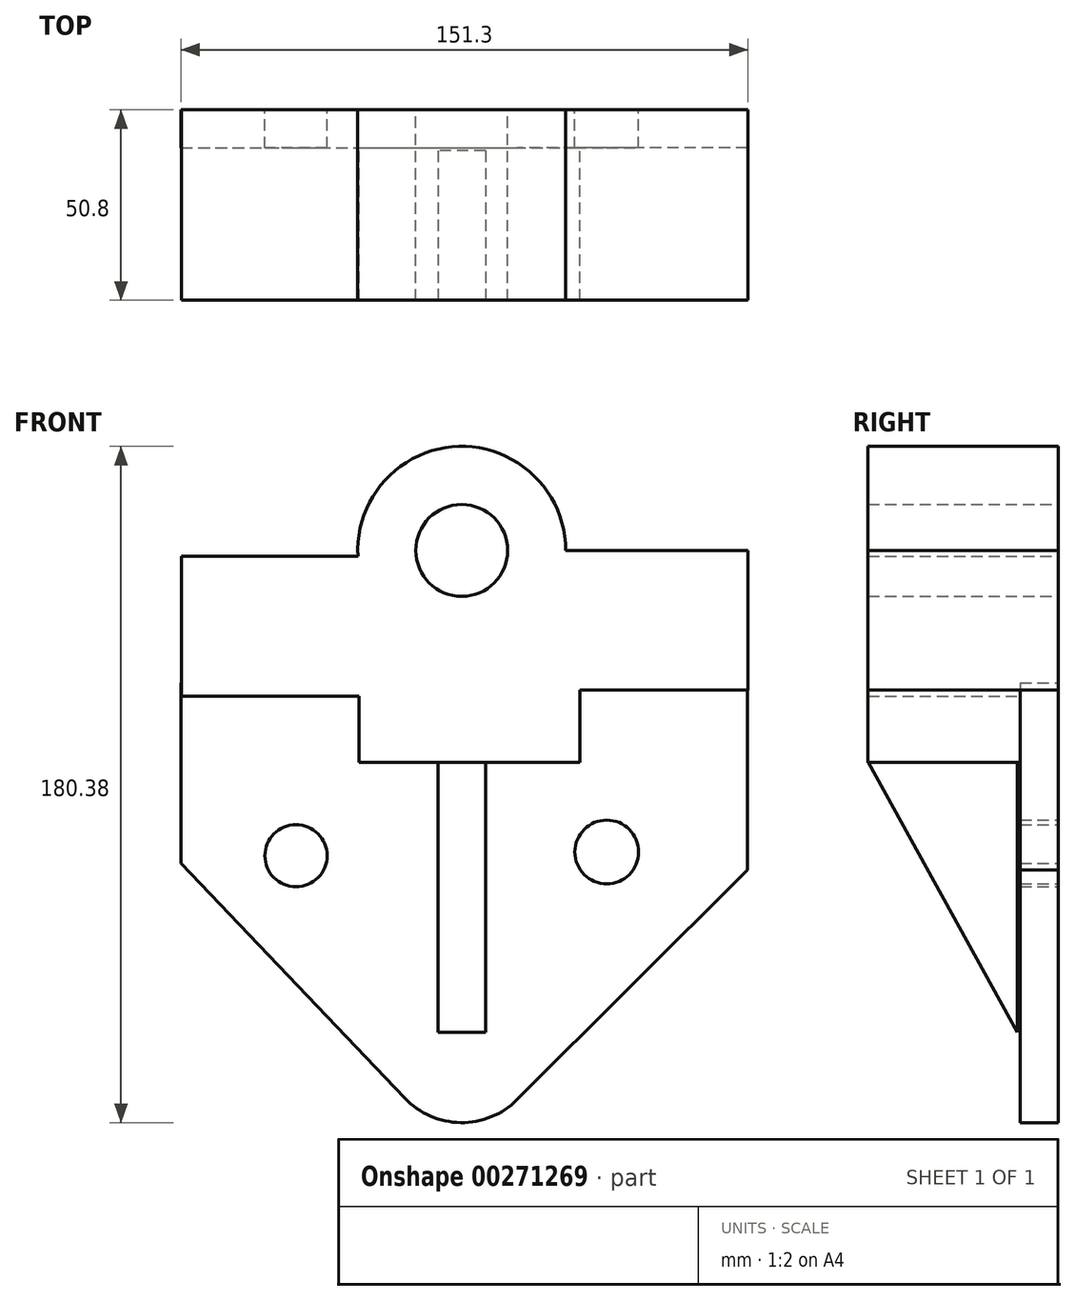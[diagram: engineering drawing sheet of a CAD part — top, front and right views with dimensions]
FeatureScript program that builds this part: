
annotation { "Feature Type Name" : "Feature", "Feature Type Description" : "" }
export const myFeature = defineFeature(function(context is Context, id is Id, definition is map)
    precondition{}
    {
        {
            var Q0;
            Q0=qCreatedBy(makeId("Front.planeOp"),FACE);
            var sketch = newSketch(context, id + "F0", { "sketchPlane" : qUnion([Q0])});
            skArc(sketch, "E0", {"start": v(27.74, 56.5) * mm, "mid": v(-0.75, 84.23) * mm, "end": v(-27.7, 54.99) * mm});
            skCircle(sketch, "E1", {"center": v(0, 56.5) * mm, "radius": 12.25 * mm});
            skLineSegment(sketch, "E2", {"start": v(27.74, 56.5) * mm, "end": v(76.4, 56.5) * mm});
            skLineSegment(sketch, "E3", {"start": v(76.4, 56.5) * mm, "end": v(76.4, 19.25) * mm});
            skLineSegment(sketch, "E4", {"start": v(76.4, 19.25) * mm, "end": v(31.51, 19.25) * mm});
            skLineSegment(sketch, "E5", {"start": v(31.51, 19.25) * mm, "end": v(31.51, 0) * mm});
            skLineSegment(sketch, "E6", {"start": v(31.51, 0) * mm, "end": v(0, 0) * mm});
            skLineSegment(sketch, "E7", {"start": v(-27.7, 54.99) * mm, "end": v(-74.78, 54.99) * mm});
            skLineSegment(sketch, "E8", {"start": v(-74.78, 54.99) * mm, "end": v(-74.78, 17.61) * mm});
            skLineSegment(sketch, "E9", {"start": v(-74.78, 17.61) * mm, "end": v(-27.36, 17.61) * mm});
            skLineSegment(sketch, "E10", {"start": v(-27.36, 17.61) * mm, "end": v(-27.36, 0) * mm});
            skLineSegment(sketch, "E11", {"start": v(-27.36, 0) * mm, "end": v(0, 0) * mm});
            skSolve(sketch);
        }
        {
            var Q0;
            Q0=makeQuery(id+"F0.imprint","IMPRINT",FACE,{"disambiguationData":[TD([[makeQuery(id+"F0.imprint","IMPRINT",EDGE,{"derivedFrom":sQuery(id+"F0.wireOp",EDGE,"E0")}),1.0]])]});
            var Q1;
            Q1 = qSketchRegion(id + "F0", true);
            extrude(context, id + "F1", {"entities" : qUnion([Q0, Q1]), "depth" : 50.8 * mm});
        }
        {
            var Q0;
            Q0=qCreatedBy(makeId("Front.planeOp"),FACE);
            var sketch = newSketch(context, id + "F2", { "sketchPlane" : qUnion([Q0])});
            skArc(sketch, "E12", {"start": v(-15.18, -89.64) * mm, "mid": v(-0.27, -96.14) * mm, "end": v(14.8, -90.02) * mm});
            skLineSegment(sketch, "E13", {"start": v(76.25, 21.22) * mm, "end": v(-74.91, 21.22) * mm});
            skLineSegment(sketch, "E14", {"start": v(-74.91, 21.22) * mm, "end": v(-74.91, -26.96) * mm});
            skLineSegment(sketch, "E15", {"start": v(-74.91, -26.96) * mm, "end": v(-15.18, -89.64) * mm});
            skLineSegment(sketch, "E16", {"start": v(76.25, 21.22) * mm, "end": v(76.25, -28.77) * mm});
            skLineSegment(sketch, "E17", {"start": v(76.25, -28.77) * mm, "end": v(14.8, -90.02) * mm});
            skCircle(sketch, "E18", {"center": v(-44.2, -24.95) * mm, "radius": 8.3 * mm});
            skCircle(sketch, "E19", {"center": v(38.71, -23.95) * mm, "radius": 8.5 * mm});
            skSolve(sketch);
        }
        {
            var Q0;
            Q0=makeQuery(id+"F2.imprint","IMPRINT",FACE,{"disambiguationData":[TD([[makeQuery(id+"F2.imprint","IMPRINT",EDGE,{"derivedFrom":sQuery(id+"F2.wireOp",EDGE,"E12")}),1.0]])]});
            extrude(context, id + "F3", {"entities" : qUnion([Q0]), "operationType" : NewBodyOperationType.ADD, "depth" : 10.16 * mm});
        }
        {
            var Q0;
            Q0=qCreatedBy(makeId("Right.planeOp"),FACE);
            var sketch = newSketch(context, id + "F4", { "sketchPlane" : qUnion([Q0])});
            skLineSegment(sketch, "E20", {"start": v(-50.74, 0) * mm, "end": v(-10.95, -72.06) * mm});
            skLineSegment(sketch, "E21", {"start": v(-10.95, -72.06) * mm, "end": v(-10.95, 0) * mm});
            skLineSegment(sketch, "E22", {"start": v(-10.95, 0) * mm, "end": v(-50.74, 0) * mm});
            skSolve(sketch);
        }
        {
            var Q0;
            Q0 = qSketchRegion(id + "F4", true);
            extrude(context, id + "F5", {"entities" : qUnion([Q0]), "operationType" : NewBodyOperationType.ADD, "endBound" : BoundingType.SYMMETRIC, "depth" : 12.7 * mm});
        }
    });
